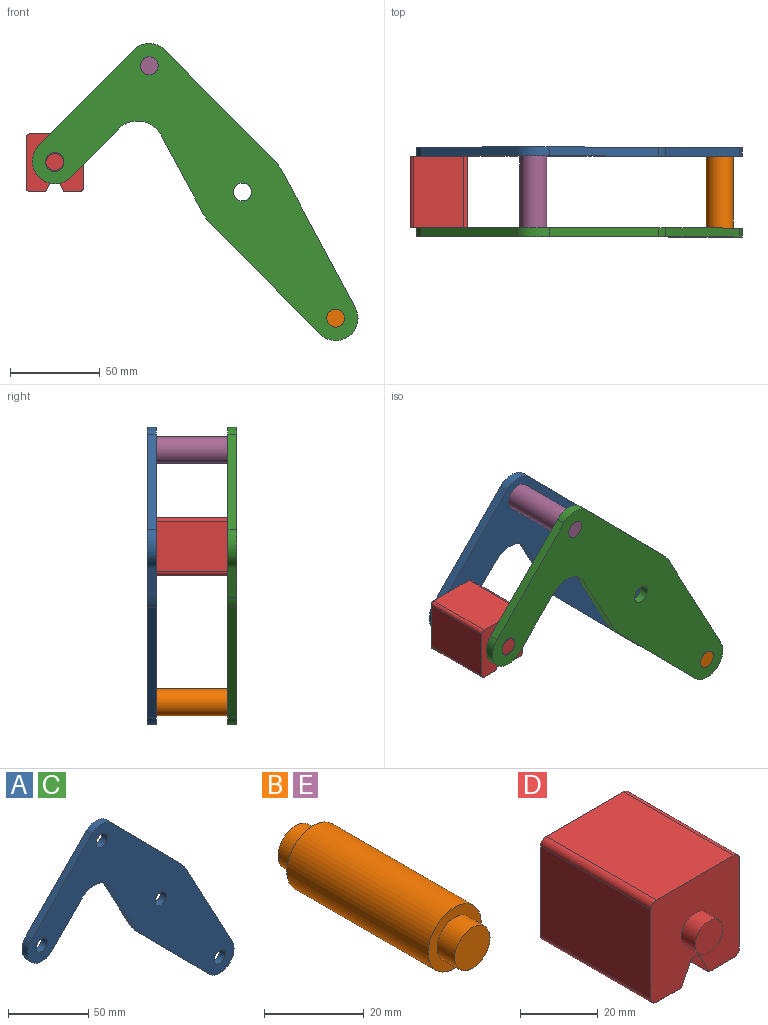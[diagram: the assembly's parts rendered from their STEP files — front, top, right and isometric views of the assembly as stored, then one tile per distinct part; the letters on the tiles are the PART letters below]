
ASSEMBLY  parts=5 mates=3
PART A: 18 faces, bbox 181.7x5x165.8 mm
  f0: plane 43.49x23.35mm, normal (-0.88,0,-0.47), area 246.8mm2, adj f1,f14,f16,f17
  f1: cylinder r=25mm len=5.75mm, axis (0,1,0), area 35.8mm2, adj f0,f2,f16,f17
  f2: plane 61.6x60.87mm, normal (-0.71,0,-0.7), area 433mm2, adj f1,f3,f16,f17
  f3: cylinder r=12.5mm len=21.39mm, axis (0,1,0), area 178.4mm2, adj f2,f4,f16,f17
  f4: plane 76.3x40.96mm, normal (0.88,0,0.47), area 433mm2, adj f3,f5,f16,f17
  f5: cylinder r=25mm len=5.75mm, axis (0,1,0), area 35.8mm2, adj f4,f6,f16,f17
  f6: plane 61.6x60.87mm, normal (0.71,0,0.7), area 433mm2, adj f5,f7,f16,f17
  f7: cylinder r=12.5mm len=17.78mm, axis (0,1,0), area 98.9mm2, adj f6,f8,f16,f17
  f8: plane 53.35x52.71mm, normal (-0.71,0,0.7), area 375mm2, adj f7,f9,f16,f17
  f9: cylinder r=12.5mm len=21.39mm, axis (0,1,0), area 196.3mm2, adj f8,f10,f16,f17
  f10: plane 26.86x26.54mm, normal (0.71,0,-0.7), area 188.8mm2, adj f9,f14,f16,f17
  f11: cylinder r=5mm len=10mm, axis (0,1,0), area 157.1mm2, adj f16,f17
  f12: cylinder r=5mm len=10mm, axis (0,1,0), area 157.1mm2, adj f16,f17
  f13: cylinder r=5mm len=10mm, axis (0,1,0), area 157.1mm2, adj f16,f17
  f14: cylinder r=15mm len=23.89mm, axis (0,1,0), area 140.2mm2, adj f0,f10,f16,f17
  f15: cylinder r=5mm len=10mm, axis (0,1,0), area 157.1mm2, adj f16,f17
  f16: plane 181.66x165.78mm, normal (0,-1,0), area 8710.1mm2, adj f0,f1,f2,f3,f4,f5,f6,f7
  f17: plane 181.66x165.78mm, normal (0,1,0), area 8710.1mm2, adj f0,f1,f2,f3,f4,f5,f6,f7
PART B: 7 faces, bbox 15x50x15 mm
  f0: cylinder r=7.5mm len=40mm, axis (0,-1,0), area 1885mm2, adj f2,f5
  f1: cylinder r=5mm len=10mm, axis (0,1,0), area 157.1mm2, adj f2,f3
  f2: plane 15x15mm, normal (0,-1,0), area 98.2mm2, adj f0,f1
  f3: plane 10x10mm, normal (0,-1,0), area 78.5mm2, adj f1
  f4: cylinder r=5mm len=10mm, axis (0,-1,0), area 157.1mm2, adj f5,f6
  f5: plane 15x15mm, normal (0,1,0), area 98.2mm2, adj f0,f4
  f6: plane 10x10mm, normal (0,1,0), area 78.5mm2, adj f4
PART C: same geometry as A
PART D: 18 faces, bbox 32.1x50x32.1 mm
  f0: plane 40x28.08mm, normal (1,0,0), area 1123.1mm2, adj f4,f10,f13,f14
  f1: plane 40x9.04mm, normal (0,0,-1), area 361.6mm2, adj f2,f4,f10,f14
  f2: plane 40x6.42mm, normal (-0.89,0,-0.45), area 287.2mm2, adj f1,f4,f10,f15
  f3: plane 40x6.42mm, normal (0.89,0,-0.45), area 287.2mm2, adj f4,f5,f10,f15
  f4: plane 32.08x32.08mm, normal (0,-1,0), area 900.6mm2, adj f0,f1,f2,f3,f5,f6,f7,f9
  f5: plane 40x9.04mm, normal (0,0,-1), area 361.6mm2, adj f3,f4,f10,f16
  f6: plane 40x28.08mm, normal (0,0,1), area 1123.1mm2, adj f4,f10,f13,f17
  f7: plane 40x28.08mm, normal (-1,0,0), area 1123.1mm2, adj f4,f10,f16,f17
  f8: plane 10x10mm, normal (0,-1,0), area 78.5mm2, adj f9
  f9: cylinder r=5mm len=10mm, axis (0,1,0), area 157.1mm2, adj f4,f8
  f10: plane 32.08x32.08mm, normal (0,1,0), area 900.6mm2, adj f0,f1,f2,f3,f5,f6,f7,f12
  f11: plane 10x10mm, normal (0,1,0), area 78.5mm2, adj f12
  f12: cylinder r=5mm len=10mm, axis (0,-1,0), area 157.1mm2, adj f10,f11
  f13: cylinder r=2mm len=40mm, axis (0,1,0), area 125.7mm2, adj f0,f4,f6,f10
  f14: cylinder r=2mm len=40mm, axis (0,-1,0), area 125.7mm2, adj f0,f1,f4,f10
  f15: cylinder r=2mm len=40mm, axis (0,1,0), area 177.1mm2, adj f2,f3,f4,f10
  f16: cylinder r=2mm len=40mm, axis (0,1,0), area 125.7mm2, adj f4,f5,f7,f10
  f17: cylinder r=2mm len=40mm, axis (0,-1,0), area 125.7mm2, adj f4,f6,f7,f10
PART E: same geometry as B
PLACE A t=(0,25,0)mm
PLACE B t=(103.95,-20,-140.78)mm
PLACE C t=(0,-20,0)mm fixed
PLACE D t=(0,-20,-0.67)mm
PLACE E t=(0,-20,0)mm
MATE fastened A.f7 <-> E.f0  axis (0,-1,0) through (-51.98,20,70.39)mm
MATE fastened B.f0 <-> C.f3  axis (0,-1,0) through (51.98,-20,-70.39)mm
MATE revolute D.f4 <-> C.f9  axis (0,-1,0) through (-104.69,-20,17.04)mm
